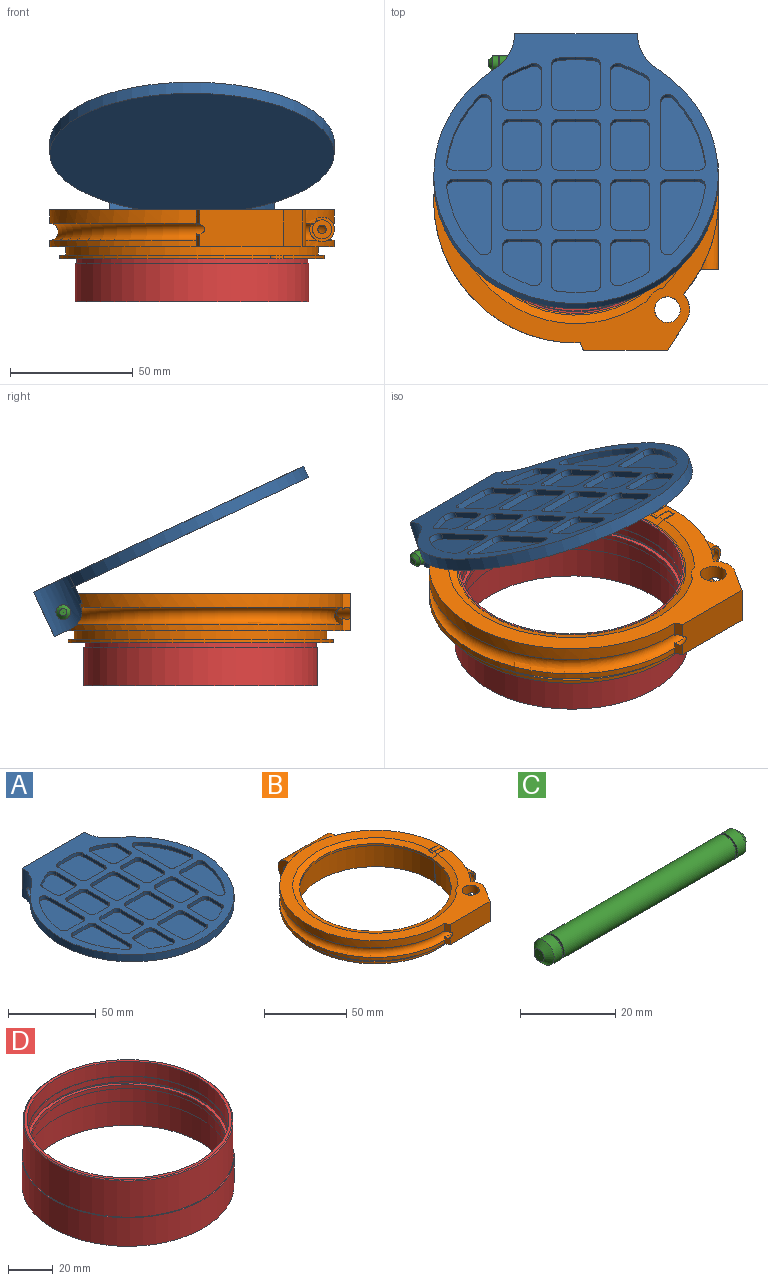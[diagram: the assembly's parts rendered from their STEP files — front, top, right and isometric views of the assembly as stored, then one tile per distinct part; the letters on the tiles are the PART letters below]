
ASSEMBLY  parts=4 mates=3
PART A: 156 faces, bbox 116x121.5x20 mm
  f0: cylinder r=58mm len=14.84mm, axis (0,0,1), area 175.4mm2, adj f1,f2,f10,f13,f154,f155
  f1: plane 17.5x9.06mm, normal (-1,0,0), area 135.4mm2, adj f0,f3,f9,f11,f13,f14,f155
  f2: cylinder r=20mm len=20mm, axis (0,0,1), area 316.9mm2, adj f0,f3,f8,f11,f13,f135,f154,f155
  f3: plane 7.5x6.55mm, normal (0,0,-1), area 41.4mm2, adj f1,f2,f11,f155
  f4: cylinder r=58mm len=14.84mm, axis (0,0,1), area 175.4mm2, adj f5,f6,f10,f12,f152,f153
  f5: plane 17.5x9.06mm, normal (1,0,0), area 135.4mm2, adj f4,f7,f9,f11,f12,f14,f153
  f6: cylinder r=20mm len=20mm, axis (0,0,1), area 316.9mm2, adj f4,f7,f8,f11,f12,f135,f152,f153
  f7: plane 7.5x6.55mm, normal (0,0,-1), area 41.4mm2, adj f5,f6,f11,f153
  f8: cylinder r=58mm len=116mm, axis (0,0,-1), area 1465.5mm2, adj f2,f6,f10,f135
  f9: cylinder r=58mm len=40mm, axis (0,0,-1), area 102.1mm2, adj f1,f5,f10,f14
  f10: plane 116x116mm, normal (0,0,-1), area 10568.3mm2, adj f0,f4,f8,f9
  f11: plane 50x20mm, normal (0,1,0), area 300mm2, adj f1,f2,f3,f5,f6,f7,f14,f135
  f12: cylinder r=3mm len=8.11mm, axis (1,0,0), area 111.5mm2, adj f4,f5,f6
  f13: cylinder r=3mm len=8.11mm, axis (1,0,0), area 111.5mm2, adj f0,f1,f2
  f14: plane 40x9.06mm, normal (0,0,-1), area 266.8mm2, adj f1,f5,f9,f11
  f15: plane 28.09x2.5mm, normal (-1,0.01,0), area 70.2mm2, adj f16,f134,f135,f136
  f16: cylinder r=3mm len=5.25mm, axis (0,0,-1), area 18.1mm2, adj f15,f17,f135,f136
  f17: cylinder r=53mm len=29.78mm, axis (0,0,-1), area 82.6mm2, adj f16,f18,f135,f136
  f18: cylinder r=3mm len=3.3mm, axis (0,0,-1), area 12.5mm2, adj f17,f19,f135,f136
  f19: plane 12.45x2.5mm, normal (0,-1,0), area 31.1mm2, adj f18,f134,f135,f136
  f20: cylinder r=3mm len=4.02mm, axis (0,0,-1), area 14.4mm2, adj f21,f119,f135,f151
  f21: cylinder r=53mm len=10.6mm, axis (0,0,-1), area 29.6mm2, adj f20,f22,f135,f151
  f22: cylinder r=3mm len=2.53mm, axis (0,0,-1), area 7.5mm2, adj f21,f23,f135,f151
  f23: plane 10.08x2.5mm, normal (1,0,0), area 25.2mm2, adj f22,f24,f135,f151
  f24: cylinder r=3mm len=3mm, axis (0,0,-1), area 11.8mm2, adj f23,f25,f135,f151
  f25: plane 10x2.5mm, normal (0,-1,0), area 25mm2, adj f24,f26,f135,f151
  f26: cylinder r=3mm len=3mm, axis (0,0,-1), area 11.8mm2, adj f25,f119,f135,f151
  f27: plane 10x2.5mm, normal (0,-1,0), area 25mm2, adj f28,f120,f135,f150
  f28: cylinder r=3mm len=3mm, axis (0,0,-1), area 11.8mm2, adj f27,f29,f135,f150
  f29: plane 17x2.5mm, normal (-1,0,0), area 42.5mm2, adj f28,f30,f135,f150
  f30: cylinder r=3mm len=3mm, axis (0,0,-1), area 11.8mm2, adj f29,f31,f135,f150
  f31: plane 10x2.5mm, normal (0,1,0), area 25mm2, adj f30,f32,f135,f150
  f32: cylinder r=3mm len=3mm, axis (0,0,-1), area 11.8mm2, adj f31,f33,f135,f150
  f33: plane 17x2.5mm, normal (1,0,0), area 42.5mm2, adj f32,f120,f135,f150
  f34: cylinder r=53mm len=14.84mm, axis (0,0,-1), area 37.2mm2, adj f35,f121,f135,f149
  f35: cylinder r=3mm len=2.97mm, axis (0,0,-1), area 10.7mm2, adj f34,f36,f135,f149
  f36: plane 17.51x2.5mm, normal (1,0,0), area 43.8mm2, adj f35,f37,f135,f149
  f37: cylinder r=3mm len=3mm, axis (0,0,-1), area 11.8mm2, adj f36,f38,f135,f149
  f38: plane 14x2.5mm, normal (0,-1,0), area 35mm2, adj f37,f39,f135,f149
  f39: cylinder r=3mm len=3mm, axis (0,0,-1), area 11.8mm2, adj f38,f40,f135,f149
  f40: plane 17.51x2.5mm, normal (-1,0,0), area 43.8mm2, adj f39,f121,f135,f149
  f41: cylinder r=3mm len=3mm, axis (0,0,-1), area 11.8mm2, adj f42,f122,f135,f148
  f42: plane 14x2.5mm, normal (0,-1,0), area 35mm2, adj f41,f43,f135,f148
  f43: cylinder r=3mm len=3mm, axis (0,0,-1), area 11.8mm2, adj f42,f44,f135,f148
  f44: plane 17x2.5mm, normal (-1,0,0), area 42.5mm2, adj f43,f45,f135,f148
  f45: cylinder r=3mm len=3mm, axis (0,0,-1), area 11.8mm2, adj f44,f46,f135,f148
  f46: plane 14x2.5mm, normal (0,1,0), area 35mm2, adj f45,f47,f135,f148
  f47: cylinder r=3mm len=3mm, axis (0,0,-1), area 11.8mm2, adj f46,f122,f135,f148
  f48: cylinder r=3mm len=2.97mm, axis (0,0,-1), area 10.7mm2, adj f49,f123,f135,f147
  f49: plane 17.51x2.5mm, normal (-1,0,0), area 43.8mm2, adj f48,f50,f135,f147
  f50: cylinder r=3mm len=3mm, axis (0,0,-1), area 11.8mm2, adj f49,f51,f135,f147
  f51: plane 14x2.5mm, normal (0,1,0), area 35mm2, adj f50,f52,f135,f147
  f52: cylinder r=3mm len=3mm, axis (0,0,-1), area 11.8mm2, adj f51,f53,f135,f147
  f53: plane 17.51x2.5mm, normal (1,0,0), area 43.8mm2, adj f52,f54,f135,f147
  f54: cylinder r=3mm len=2.97mm, axis (0,0,-1), area 10.7mm2, adj f53,f123,f135,f147
  f55: plane 10.08x2.5mm, normal (-1,0,0), area 25.2mm2, adj f56,f124,f135,f146
  f56: cylinder r=3mm len=3mm, axis (0,0,-1), area 11.8mm2, adj f55,f57,f135,f146
  f57: plane 10x2.5mm, normal (0,1,0), area 25mm2, adj f56,f58,f135,f146
  f58: cylinder r=3mm len=3mm, axis (0,0,-1), area 11.8mm2, adj f57,f59,f135,f146
  f59: plane 15.02x2.5mm, normal (1,0,0), area 37.6mm2, adj f58,f60,f135,f146
  f60: cylinder r=3mm len=4.02mm, axis (0,0,-1), area 14.4mm2, adj f59,f61,f135,f146
  f61: cylinder r=53mm len=10.6mm, axis (0,0,-1), area 29.6mm2, adj f60,f124,f135,f146
  f62: plane 12.45x2.5mm, normal (0,1,0), area 31.1mm2, adj f63,f125,f135,f145
  f63: cylinder r=3mm len=3.02mm, axis (0,0,-1), area 11.8mm2, adj f62,f64,f135,f145
  f64: plane 28.09x2.5mm, normal (1,-0.01,0), area 70.2mm2, adj f63,f65,f135,f145
  f65: cylinder r=3mm len=5.25mm, axis (0,0,-1), area 18.1mm2, adj f64,f66,f135,f145
  f66: cylinder r=53mm len=29.78mm, axis (0,0,-1), area 82.6mm2, adj f65,f125,f135,f145
  f67: cylinder r=3mm len=4.02mm, axis (0,0,-1), area 14.4mm2, adj f68,f126,f135,f144
  f68: plane 15.02x2.5mm, normal (-1,0,0), area 37.6mm2, adj f67,f69,f135,f144
  f69: cylinder r=3mm len=3mm, axis (0,0,-1), area 11.8mm2, adj f68,f70,f135,f144
  f70: plane 10x2.5mm, normal (0,1,0), area 25mm2, adj f69,f71,f135,f144
  f71: cylinder r=3mm len=3mm, axis (0,0,-1), area 11.8mm2, adj f70,f72,f135,f144
  f72: plane 10.08x2.5mm, normal (1,0,0), area 25.2mm2, adj f71,f73,f135,f144
  f73: cylinder r=3mm len=2.53mm, axis (0,0,-1), area 7.5mm2, adj f72,f126,f135,f144
  f74: plane 17x2.5mm, normal (-1,0,0), area 42.5mm2, adj f75,f127,f135,f143
  f75: cylinder r=3mm len=3mm, axis (0,0,-1), area 11.8mm2, adj f74,f76,f135,f143
  f76: plane 10x2.5mm, normal (0,1,0), area 25mm2, adj f75,f77,f135,f143
  f77: cylinder r=3mm len=3mm, axis (0,0,-1), area 11.8mm2, adj f76,f78,f135,f143
  f78: plane 17x2.5mm, normal (1,0,0), area 42.5mm2, adj f77,f79,f135,f143
  f79: cylinder r=3mm len=3mm, axis (0,0,-1), area 11.8mm2, adj f78,f80,f135,f143
  f80: plane 10x2.5mm, normal (0,-1,0), area 25mm2, adj f79,f127,f135,f143
  f81: cylinder r=3mm len=3mm, axis (0,0,-1), area 11.8mm2, adj f82,f128,f135,f142
  f82: plane 17x2.5mm, normal (-1,0,0), area 42.5mm2, adj f81,f83,f135,f142
  f83: cylinder r=3mm len=3mm, axis (0,0,-1), area 11.8mm2, adj f82,f84,f135,f142
  f84: plane 14x2.5mm, normal (0,1,0), area 35mm2, adj f83,f85,f135,f142
  f85: cylinder r=3mm len=3mm, axis (0,0,-1), area 11.8mm2, adj f84,f86,f135,f142
  f86: plane 17x2.5mm, normal (1,0,0), area 42.5mm2, adj f85,f87,f135,f142
  f87: cylinder r=3mm len=3mm, axis (0,0,-1), area 11.8mm2, adj f86,f128,f135,f142
  f88: cylinder r=53mm len=29.78mm, axis (0,0,-1), area 82.6mm2, adj f89,f129,f135,f141
  f89: cylinder r=3mm len=5.25mm, axis (0,0,-1), area 18.1mm2, adj f88,f90,f135,f141
  f90: plane 28.09x2.5mm, normal (-1,-0.01,0), area 70.2mm2, adj f89,f91,f135,f141
  f91: cylinder r=3mm len=3.02mm, axis (0,0,-1), area 11.8mm2, adj f90,f92,f135,f141
  f92: plane 12.45x2.5mm, normal (0,1,0), area 31.1mm2, adj f91,f129,f135,f141
  f93: cylinder r=3mm len=3mm, axis (0,0,-1), area 11.8mm2, adj f94,f130,f135,f140
  f94: plane 17x2.5mm, normal (1,0,0), area 42.5mm2, adj f93,f95,f135,f140
  f95: cylinder r=3mm len=3mm, axis (0,0,-1), area 11.8mm2, adj f94,f96,f135,f140
  f96: plane 10x2.5mm, normal (0,-1,0), area 25mm2, adj f95,f97,f135,f140
  f97: cylinder r=3mm len=3mm, axis (0,0,-1), area 11.8mm2, adj f96,f98,f135,f140
  f98: plane 17x2.5mm, normal (-1,0,0), area 42.5mm2, adj f97,f99,f135,f140
  f99: cylinder r=3mm len=3mm, axis (0,0,-1), area 11.8mm2, adj f98,f130,f135,f140
  f100: cylinder r=3mm len=2.53mm, axis (0,0,-1), area 7.5mm2, adj f101,f131,f135,f139
  f101: cylinder r=53mm len=10.6mm, axis (0,0,-1), area 29.6mm2, adj f100,f102,f135,f139
  f102: cylinder r=3mm len=4.02mm, axis (0,0,-1), area 14.4mm2, adj f101,f103,f135,f139
  f103: plane 15.02x2.5mm, normal (1,0,0), area 37.6mm2, adj f102,f104,f135,f139
  f104: cylinder r=3mm len=3mm, axis (0,0,-1), area 11.8mm2, adj f103,f105,f135,f139
  f105: plane 10x2.5mm, normal (0,-1,0), area 25mm2, adj f104,f106,f135,f139
  f106: cylinder r=3mm len=3mm, axis (0,0,-1), area 11.8mm2, adj f105,f131,f135,f139
  f107: cylinder r=3mm len=3mm, axis (0,0,-1), area 11.8mm2, adj f108,f132,f135,f138
  f108: plane 10x2.5mm, normal (0,-1,0), area 25mm2, adj f107,f109,f135,f138
  f109: cylinder r=3mm len=3mm, axis (0,0,-1), area 11.8mm2, adj f108,f110,f135,f138
  f110: plane 17x2.5mm, normal (-1,0,0), area 42.5mm2, adj f109,f111,f135,f138
  f111: cylinder r=3mm len=3mm, axis (0,0,-1), area 11.8mm2, adj f110,f112,f135,f138
  f112: plane 10x2.5mm, normal (0,1,0), area 25mm2, adj f111,f113,f135,f138
  f113: cylinder r=3mm len=3mm, axis (0,0,-1), area 11.8mm2, adj f112,f132,f135,f138
  f114: plane 12.45x2.5mm, normal (0,-1,0), area 31.1mm2, adj f115,f133,f135,f137
  f115: cylinder r=3mm len=3.3mm, axis (0,0,-1), area 12.5mm2, adj f114,f116,f135,f137
  f116: cylinder r=53mm len=29.78mm, axis (0,0,-1), area 82.6mm2, adj f115,f117,f135,f137
  f117: cylinder r=3mm len=5.25mm, axis (0,0,-1), area 18.1mm2, adj f116,f118,f135,f137
  f118: plane 28.09x2.5mm, normal (1,0.01,0), area 70.2mm2, adj f117,f133,f135,f137
  f119: plane 15.02x2.5mm, normal (-1,0,0), area 37.6mm2, adj f20,f26,f135,f151
  f120: cylinder r=3mm len=3mm, axis (0,0,-1), area 11.8mm2, adj f27,f33,f135,f150
  f121: cylinder r=3mm len=2.97mm, axis (0,0,-1), area 10.7mm2, adj f34,f40,f135,f149
  f122: plane 17x2.5mm, normal (1,0,0), area 42.5mm2, adj f41,f47,f135,f148
  f123: cylinder r=53mm len=14.84mm, axis (0,0,-1), area 37.2mm2, adj f48,f54,f135,f147
  f124: cylinder r=3mm len=2.53mm, axis (0,0,-1), area 7.5mm2, adj f55,f61,f135,f146
  f125: cylinder r=3mm len=3.3mm, axis (0,0,-1), area 12.5mm2, adj f62,f66,f135,f145
  f126: cylinder r=53mm len=10.6mm, axis (0,0,-1), area 29.6mm2, adj f67,f73,f135,f144
  f127: cylinder r=3mm len=3mm, axis (0,0,-1), area 11.8mm2, adj f74,f80,f135,f143
  f128: plane 14x2.5mm, normal (0,-1,0), area 35mm2, adj f81,f87,f135,f142
  f129: cylinder r=3mm len=3.3mm, axis (0,0,-1), area 12.5mm2, adj f88,f92,f135,f141
  f130: plane 10x2.5mm, normal (0,1,0), area 25mm2, adj f93,f99,f135,f140
  f131: plane 10.08x2.5mm, normal (-1,0,0), area 25.2mm2, adj f100,f106,f135,f139
  f132: plane 17x2.5mm, normal (1,0,0), area 42.5mm2, adj f107,f113,f135,f138
  f133: cylinder r=3mm len=3.02mm, axis (0,0,-1), area 11.8mm2, adj f114,f118,f135,f137
  f134: cylinder r=3mm len=3.02mm, axis (0,0,-1), area 11.8mm2, adj f15,f19,f135,f136
  f135: plane 121.5x116mm, normal (0,0,1), area 4643.1mm2, adj f2,f6,f8,f11,f15,f16,f17,f18
  f136: plane 34.09x18.45mm, normal (0,0,1), area 467.7mm2, adj f15,f16,f17,f18,f19,f134
  f137: plane 34.09x18.45mm, normal (0,0,1), area 467.7mm2, adj f114,f115,f116,f117,f118,f133
  f138: plane 23x16mm, normal (0,0,1), area 360.3mm2, adj f107,f108,f109,f110,f111,f112,f113,f132
  f139: plane 21.02x16mm, normal (0,0,1), area 295mm2, adj f100,f101,f102,f103,f104,f105,f106,f131
  f140: plane 23x16mm, normal (0,0,1), area 360.3mm2, adj f93,f94,f95,f96,f97,f98,f99,f130
  f141: plane 34.09x18.45mm, normal (0,0,1), area 467.7mm2, adj f88,f89,f90,f91,f92,f129
  f142: plane 23x20mm, normal (0,0,1), area 452.3mm2, adj f81,f82,f83,f84,f85,f86,f87,f128
  f143: plane 23x16mm, normal (0,0,1), area 360.3mm2, adj f74,f75,f76,f77,f78,f79,f80,f127
  f144: plane 21.02x16mm, normal (0,0,1), area 295mm2, adj f67,f68,f69,f70,f71,f72,f73,f126
  f145: plane 34.09x18.45mm, normal (0,0,1), area 467.7mm2, adj f62,f63,f64,f65,f66,f125
  f146: plane 21.02x16mm, normal (0,0,1), area 295mm2, adj f55,f56,f57,f58,f59,f60,f61,f124
  f147: plane 24x20mm, normal (0,0,1), area 467.2mm2, adj f48,f49,f50,f51,f52,f53,f54,f123
  f148: plane 23x20mm, normal (0,0,1), area 452.3mm2, adj f41,f42,f43,f44,f45,f46,f47,f122
  f149: plane 24x20mm, normal (0,0,1), area 467.2mm2, adj f34,f35,f36,f37,f38,f39,f40,f121
  f150: plane 23x16mm, normal (0,0,1), area 360.3mm2, adj f27,f28,f29,f30,f31,f32,f33,f120
  f151: plane 21.02x16mm, normal (0,0,1), area 295mm2, adj f20,f21,f22,f23,f24,f25,f26,f119
  f152: plane 1.65x1.13mm, normal (0,0,-1), area 0.1mm2, adj f4,f6,f153
  f153: cylinder r=7.5mm len=12.01mm, axis (1,0,0), area 31.4mm2, adj f4,f5,f6,f7,f152
  f154: plane 1.65x1.13mm, normal (0,0,-1), area 0.1mm2, adj f0,f2,f155
  f155: cylinder r=7.5mm len=12.01mm, axis (1,0,0), area 31.4mm2, adj f0,f1,f2,f3,f154
PART B: 75 faces, bbox 130.9x131x20.1 mm
  f0: cylinder r=54mm len=35.88mm, axis (0,0,1), area 60.8mm2, adj f18,f22,f44,f74
  f1: cylinder r=2.5mm len=6.74mm, axis (-0.91,-0.42,0), area 62mm2, adj f65,f73
  f2: torus R=58mm, axis (0,0,1), area 2702.4mm2, adj f3,f9,f11,f13,f30,f31,f43,f53
  f3: cylinder r=58mm len=28.3mm, axis (0,0,1), area 145.3mm2, adj f2,f7,f66,f68,f71
  f4: plane 6.22x3.02mm, normal (-0.91,-0.42,0), area 19mm2, adj f11,f38,f67,f69,f71
  f5: cylinder r=58mm len=41.13mm, axis (0,0,1), area 107.8mm2, adj f15,f17,f26,f41,f45,f65
  f6: cylinder r=58mm len=41.13mm, axis (0,0,1), area 208.8mm2, adj f15,f32,f38,f41,f42,f45,f58,f65
  f7: torus R=58mm, axis (0,0,1), area 30.7mm2, adj f3,f66,f72
  f8: cylinder r=58mm len=30.2mm, axis (0,0,1), area 4.4mm2, adj f26,f62
  f9: cylinder r=58mm len=114mm, axis (0,0,1), area 409mm2, adj f2,f26,f61,f62,f68
  f10: cylinder r=58mm len=30.2mm, axis (0,0,1), area 4.4mm2, adj f38,f62
  f11: cylinder r=58mm len=116mm, axis (0,0,1), area 1293.2mm2, adj f2,f4,f14,f31,f38,f43,f53,f60
  f12: cylinder r=1.7mm len=22.2mm, axis (0,1,0), area 131.9mm2, adj f16,f44,f59
  f13: cylinder r=58mm len=52.7mm, axis (0,0,1), area 168.9mm2, adj f2,f26,f53,f60,f62
  f14: torus R=58mm, axis (0,0,1), area 1.5mm2, adj f11,f31,f53
  f15: torus R=58mm, axis (0,0,1), area 137.7mm2, adj f5,f6,f41,f42,f58,f65
  f16: torus R=58mm, axis (0,0,1), area 44.1mm2, adj f12,f44
  f17: torus R=58mm, axis (0,0,1), area 31.1mm2, adj f5,f41,f45
  f18: plane 108x108mm, normal (0,0,-1), area 1897.7mm2, adj f0,f20,f33,f34,f44,f50,f51,f52
  f19: plane 4.82x2.85mm, normal (0,0,-1), area 13.6mm2, adj f21,f45,f46,f47
  f20: cylinder r=54mm len=108mm, axis (0,0,1), area 428.4mm2, adj f18,f22,f53,f74
  f21: cylinder r=54mm len=2.85mm, axis (0,0,1), area 4.3mm2, adj f19,f23,f45,f46
  f22: plane 108x107.9mm, normal (0,0,1), area 806.5mm2, adj f0,f20,f24,f44,f53,f74
  f23: plane 2.85x2.59mm, normal (0,0,1), area 7.1mm2, adj f21,f25,f45,f46
  f24: cylinder r=51.5mm len=103mm, axis (0,0,1), area 1109.4mm2, adj f22,f26,f44,f53
  f25: cylinder r=51.5mm len=3.5mm, axis (0,0,1), area 10mm2, adj f23,f26,f45,f46
  f26: plane 119x116mm, normal (0,0,-1), area 2513.1mm2, adj f5,f8,f9,f13,f24,f25,f44,f45
  f27: plane 5.55x2.85mm, normal (0,0,1), area 15.7mm2, adj f28,f49,f51,f52
  f28: cone r=46mm half-angle=70deg, axis (0,0,1), area 1312.2mm2, adj f27,f38,f39,f44,f50,f51,f52,f53
  f29: cone r=46mm half-angle=70deg, axis (0,0,1), area 2.7mm2, adj f38,f45,f46,f47
  f30: cylinder r=1.7mm len=11.7mm, axis (0,1,0), area 35.9mm2, adj f2,f43,f53
  f31: cylinder r=5mm len=11.7mm, axis (0,1,0), area 95.3mm2, adj f2,f11,f14,f43,f53
  f32: torus R=58mm, axis (0,0,1), area 5.6mm2, adj f6,f41,f45
  f33: cylinder r=48mm len=96mm, axis (0,0,1), area 5122mm2, adj f18,f40,f44,f52
  f34: cylinder r=54mm len=2.85mm, axis (0,0,1), area 4.3mm2, adj f18,f35,f51,f52
  f35: plane 2.85x2.59mm, normal (0,0,1), area 7.1mm2, adj f34,f36,f51,f52
  f36: cylinder r=51.5mm len=3.5mm, axis (0,0,1), area 10mm2, adj f35,f37,f51,f52
  f37: plane 4.17x2.85mm, normal (0,0,-1), area 11.7mm2, adj f36,f49,f51,f52
  f38: plane 119x116mm, normal (0,0,1), area 2954.2mm2, adj f4,f6,f10,f11,f28,f29,f44,f45
  f39: cylinder r=46mm len=92mm, axis (0,0,1), area 433.1mm2, adj f28,f40,f44,f52
  f40: plane 96x96mm, normal (0,0,-1), area 590mm2, adj f33,f39,f44,f52
  f41: cylinder r=5mm len=31mm, axis (0,1,0), area 340.7mm2, adj f5,f6,f15,f17,f32,f42,f45
  f42: plane 10.03x10.03mm, normal (0,-1,0), area 28.1mm2, adj f6,f15,f41,f58
  f43: plane 8.45x5.58mm, normal (0,1,0), area 25.2mm2, adj f2,f11,f30,f31
  f44: plane 20.01x10.01mm, normal (0,1,0), area 144mm2, adj f0,f12,f16,f18,f22,f24,f26,f28
  f45: plane 20.01x8.83mm, normal (0,1,0), area 142.7mm2, adj f5,f6,f17,f19,f21,f23,f25,f26
  f46: plane 20x6.7mm, normal (0,-1,0), area 115.6mm2, adj f19,f21,f23,f25,f26,f29,f38,f47
  f47: plane 19.74x2.89mm, normal (-1,0,0), area 56.1mm2, adj f19,f29,f45,f46
  f48: plane 15x3.45mm, normal (-1,0,0), area 51.8mm2, adj f26,f38,f44,f46
  f49: plane 15x2.85mm, normal (1,0,0), area 42.8mm2, adj f27,f37,f51,f52
  f50: plane 19.66x3.52mm, normal (1,0,0), area 67.5mm2, adj f18,f28,f51,f53
  f51: plane 20x6.7mm, normal (0,1,0), area 117mm2, adj f18,f27,f28,f34,f35,f36,f37,f49
  f52: plane 20.01x9.69mm, normal (0,-1,0), area 139.2mm2, adj f18,f27,f28,f33,f34,f35,f36,f37
  f53: plane 20.01x9.13mm, normal (0,-1,0), area 148.3mm2, adj f2,f11,f13,f14,f18,f20,f22,f24
  f54: cylinder r=1.7mm len=2.85mm, axis (0,1,0), area 3.2mm2, adj f45,f46,f55
  f55: torus R=58mm, axis (0,0,1), area 3.2mm2, adj f45,f46,f54
  f56: cylinder r=1.7mm len=2.85mm, axis (0,1,0), area 3.2mm2, adj f51,f52,f57
  f57: torus R=58mm, axis (0,0,1), area 3.2mm2, adj f51,f52,f56
  f58: cylinder r=3.9mm len=7.8mm, axis (0,-1,0), area 62.1mm2, adj f6,f15,f42,f59
  f59: plane 7.8x7.8mm, normal (0,-1,0), area 38.7mm2, adj f12,f58
  f60: plane 15x12.81mm, normal (1,0,0), area 104.1mm2, adj f2,f11,f13,f62,f63
  f61: plane 15x12.81mm, normal (-1,0,0), area 104.1mm2, adj f2,f9,f11,f62,f63
  f62: cylinder r=7.5mm len=40mm, axis (-1,0,0), area 876.4mm2, adj f8,f9,f10,f11,f13,f60,f61
  f63: cylinder r=3mm len=40mm, axis (-1,0,0), area 478.3mm2, adj f2,f11,f60,f61
  f64: cylinder r=9mm len=6.19mm, axis (0,0,1), area 2.3mm2, adj f28,f38
  f65: cylinder r=9mm len=15mm, axis (0,0,1), area 181.7mm2, adj f1,f5,f6,f15,f26,f38,f70
  f66: cylinder r=9mm len=7mm, axis (0,0,1), area 7.8mm2, adj f2,f3,f7,f72
  f67: cylinder r=58mm len=4.9mm, axis (0,0,1), area 1mm2, adj f2,f4,f71
  f68: plane 5.22x3.02mm, normal (-0.91,-0.42,0), area 15.7mm2, adj f3,f9,f26,f69,f71
  f69: plane 34.21x15mm, normal (0,-1,0), area 507.4mm2, adj f4,f26,f38,f68,f70,f71
  f70: plane 15x11.68mm, normal (0.84,-0.54,0), area 208.7mm2, adj f26,f38,f65,f69
  f71: cylinder r=2.5mm len=15.76mm, axis (-0.91,-0.42,0), area 86.8mm2, adj f3,f4,f67,f68,f69
  f72: cylinder r=2.5mm len=28.88mm, axis (-0.91,-0.42,0), area 245.4mm2, adj f2,f7,f66,f73
  f73: cylinder r=5.25mm len=15mm, axis (0,0,1), area 453.2mm2, adj f1,f26,f38,f72
  f74: cylinder r=5.25mm len=5.02mm, axis (0,0,1), area 10.6mm2, adj f0,f18,f20,f22
PART C: 13 faces, bbox 60x6x6 mm
  f0: cylinder r=3mm len=51mm, axis (1,0,0), area 961.3mm2, adj f1,f12
  f1: plane 6x6mm, normal (-1,0,0), area 8.6mm2, adj f0,f2
  f2: cylinder r=2.5mm len=5mm, axis (1,0,0), area 7.9mm2, adj f1,f3
  f3: plane 6x6mm, normal (1,0,0), area 8.6mm2, adj f2,f4
  f4: cylinder r=3mm len=6mm, axis (1,0,0), area 47.1mm2, adj f3,f5
  f5: cone r=3mm half-angle=45deg, axis (1,0,0), area 30mm2, adj f4,f6
  f6: cone r=1.5mm half-angle=89.9deg, axis (1,0,0), area 7.1mm2, adj f5
  f7: cone r=1.5mm half-angle=89.9deg, axis (-1,0,0), area 7.1mm2, adj f8
  f8: cone r=3mm half-angle=45deg, axis (-1,0,0), area 30mm2, adj f7,f9
  f9: cylinder r=3mm len=6mm, axis (1,0,0), area 47.1mm2, adj f8,f10
  f10: plane 6x6mm, normal (-1,0,0), area 8.6mm2, adj f9,f11
  f11: cylinder r=2.5mm len=5mm, axis (1,0,0), area 7.9mm2, adj f10,f12
  f12: plane 6x6mm, normal (1,0,0), area 8.6mm2, adj f0,f11
PART D: 17 faces, bbox 95.2x95.2x36 mm
  f0: plane 93.32x93.32mm, normal (0,0,1), area 412.6mm2, adj f1,f16
  f1: cylinder r=45.23mm len=90.46mm, axis (0,0,1), area 2273.5mm2, adj f0,f2
  f2: plane 90.46x90.46mm, normal (0,0,1), area 65.2mm2, adj f1,f3
  f3: cylinder r=45mm len=90mm, axis (0,0,1), area 848.2mm2, adj f2,f4
  f4: plane 91x91mm, normal (0,0,-1), area 142.2mm2, adj f3,f5
  f5: cylinder r=45.5mm len=91mm, axis (0,0,1), area 284.5mm2, adj f4,f6
  f6: plane 91x91mm, normal (0,0,1), area 421.8mm2, adj f5,f7
  f7: cylinder r=44mm len=88mm, axis (0,0,1), area 554.3mm2, adj f6,f8
  f8: plane 91x91mm, normal (0,0,-1), area 421.8mm2, adj f7,f9
  f9: cylinder r=45.5mm len=91mm, axis (0,0,1), area 2287.1mm2, adj f8,f10
  f10: plane 93x93mm, normal (0,0,-1), area 289mm2, adj f9,f11
  f11: cylinder r=46.5mm len=93mm, axis (0,0,1), area 4090.4mm2, adj f10,f12
  f12: plane 95.2x95.2mm, normal (0,0,-1), area 325.2mm2, adj f11,f13
  f13: cylinder r=47.6mm len=95.2mm, axis (0,0,1), area 4694.7mm2, adj f12,f14
  f14: plane 95.2x95.2mm, normal (0,0,1), area 133.9mm2, adj f13,f15
  f15: cylinder r=47.15mm len=94.3mm, axis (0,0,1), area 5869.3mm2, adj f14,f16
  f16: cone r=46.66mm half-angle=45deg, axis (0,0,-1), area 204.6mm2, adj f0,f15
PLACE A rot(axis=(-1,0,0),25deg) t=(-6.52,37.49,-4.95)mm
PLACE B t=(-6.52,30.34,-28.2)mm
PLACE C t=(-12.02,86.34,-32.7)mm
PLACE D t=(-6.52,30.34,-26.7)mm
MATE fastened B.f0 <-> D.f1  axis (0,0,1) through (-6.52,30.34,-26.7)mm
MATE fastened C.f0 <-> B.f62  axis (1,0,0) through (13.48,86.34,-32.7)mm
MATE revolute A.f12 <-> B.f62  axis (1,0,0) through (-26.52,86.34,-32.7)mm
